# Revit family: 873-00-001-DN200-300
name_source: partatom
category: Pipe Accessories
units: mm (PartAtom-declared; Revit-internal decimal feet)

## family parameters
Always vertical = Yes
Cut with Voids When Loaded = No
Part Type = Valve - Breaks Into
Round Connector Dimension = Use Diameter
Shared = No
Work Plane-Based = No

## types (5) — shared parameters
873-0200-00-141000 = DN200_PN16
873-0250-00-041000 = DN250_PN10
873-0250-00-141000 = DN250_PN16
873-0300-00-041000 = DN300_PN10
Body_Wallthicknss = 10 mm  [stored 0.0328084 ft]
Description_ = AVK DISMANTLING JOINT
Flange_thickness = 20 mm  [stored 0.0656168 ft]
Search_table = 873-00-001-DN200-300
URL product pages = https://www.avkvalves.com

## per-type parameters (varying)
| type | 873-0300-00-141000 | A | DN | Id(Radius) | L | T | d1 | d2 |
| DN200_PN16 | DN300_PN10 | 210 mm  [stored 0.688976 ft] | 200 mm  [stored 0.656168 ft] | 100 mm  [stored 0.328084 ft] | 350 mm  [stored 1.14829 ft] | 20 mm  [stored 0.0656168 ft] | 295 mm  [stored 0.967848 ft] | 170 mm  [stored 0.557743 ft] |
| DN250_PN10 | DN300_PN10 | 225 mm  [stored 0.738189 ft] | 250 mm  [stored 0.82021 ft] | 125 mm  [stored 0.410105 ft] | 370 mm  [stored 1.21391 ft] | 20 mm  [stored 0.0656168 ft] | 350 mm  [stored 1.14829 ft] | 200 mm  [stored 0.656168 ft] |
| DN250_PN16 | DN300_PN10 | 225 mm  [stored 0.738189 ft] | 250 mm  [stored 0.82021 ft] | 125 mm  [stored 0.410105 ft] | 380 mm | 24 mm  [stored 0.0787402 ft] | 355 mm | 200 mm  [stored 0.656168 ft] |
| DN300_PN10 | DN300_PN16 | 240 mm  [stored 0.787402 ft] | 300 mm  [stored 0.984252 ft] | 150 mm | 390 mm  [stored 1.27953 ft] | 20 mm  [stored 0.0656168 ft] | 400 mm  [stored 1.31234 ft] | 228 mm |
| DN300_PN16 | DN300_PN16 | 240 mm  [stored 0.787402 ft] | 300 mm  [stored 0.984252 ft] | 150 mm | 400 mm  [stored 1.31234 ft] | 24 mm  [stored 0.0787402 ft] | 410 mm  [stored 1.34514 ft] | 228 mm |

note: [stored X ft] marks values corroborated as IEEE doubles in the binary element streams (Revit-internal decimal feet)

## geometry (parser evidence)
native form markers: Sweep x7
no freeform markers — native parametric forms only
